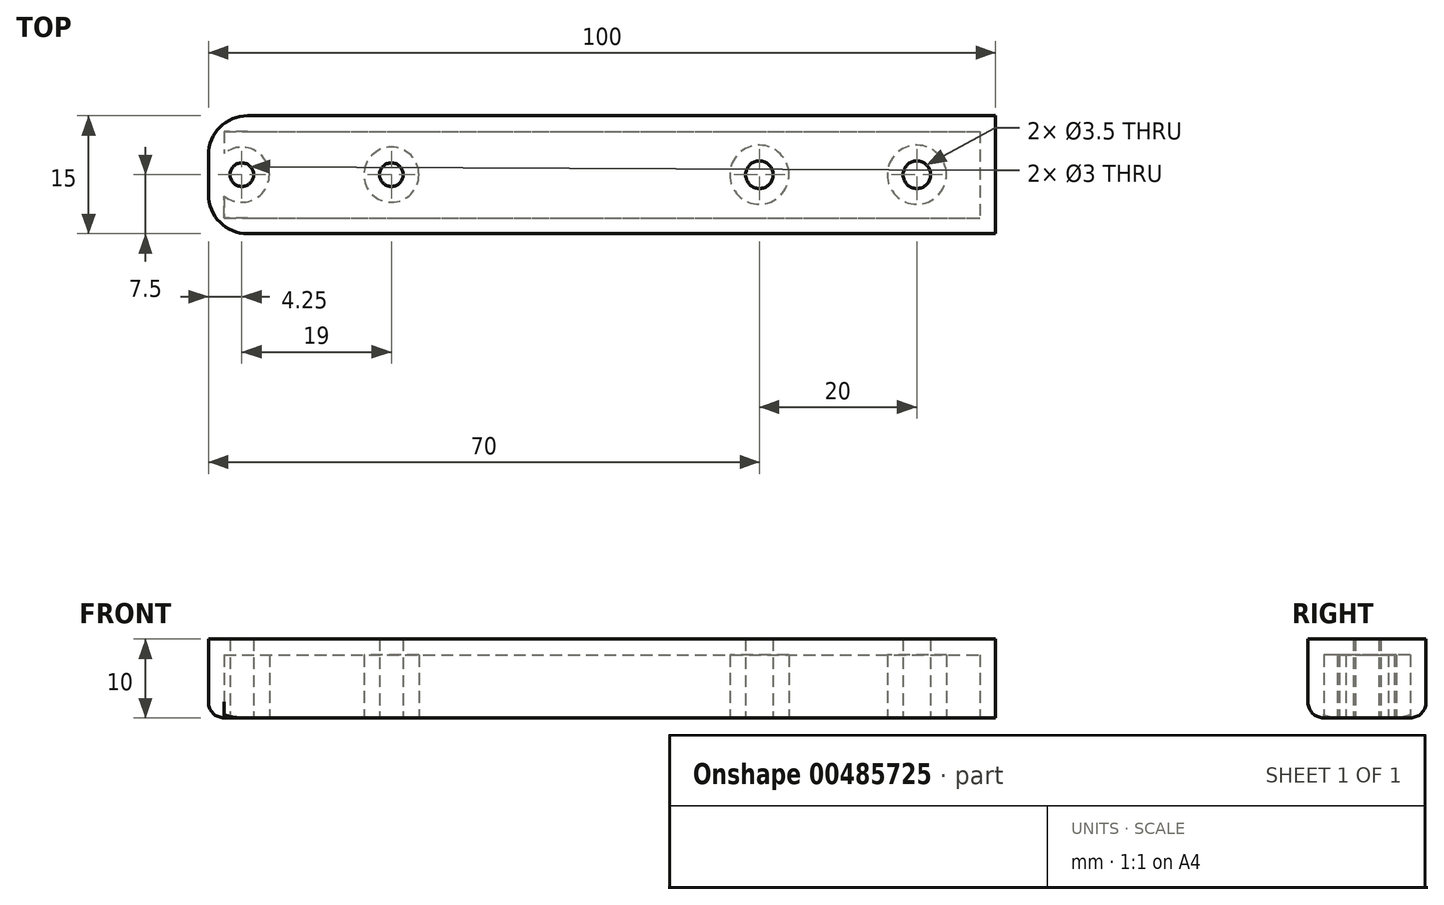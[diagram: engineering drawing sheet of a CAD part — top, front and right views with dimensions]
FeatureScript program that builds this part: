
annotation { "Feature Type Name" : "Feature", "Feature Type Description" : "" }
export const myFeature = defineFeature(function(context is Context, id is Id, definition is map)
    precondition{}
    {
        {
            var Q0;
            Q0=qCreatedBy(makeId("Top.planeOp"),FACE);
            var sketch = newSketch(context, id + "F0", { "sketchPlane" : qUnion([Q0])});
            skLineSegment(sketch, "E0.bottom", {"start": v(-50, 7.5) * mm, "end": v(50, 7.5) * mm});
            skLineSegment(sketch, "E0.top", {"start": v(-50, -7.5) * mm, "end": v(50, -7.5) * mm});
            skLineSegment(sketch, "E0.left", {"start": v(-50, 7.5) * mm, "end": v(-50, -7.5) * mm});
            skLineSegment(sketch, "E0.right", {"start": v(50, 7.5) * mm, "end": v(50, -7.5) * mm});
            skPoint(sketch, "E0.middle", {"position": v(0, 0) * mm});
            skCircle(sketch, "E1", {"center": v(40, 0) * mm, "radius": 1.75 * mm});
            skCircle(sketch, "E2", {"center": v(20, 0) * mm, "radius": 1.75 * mm});
            skCircle(sketch, "E3", {"center": v(-45.75, 0) * mm, "radius": 1.5 * mm});
            skCircle(sketch, "E4", {"center": v(-26.75, 0) * mm, "radius": 1.5 * mm});
            skLineSegment(sketch, "E5", {"start": v(10, 7.5) * mm, "end": v(10, -7.5) * mm});
            skSolve(sketch);
        }
        {
            var Q0;
            Q0=makeQuery(id+"F0.imprint","IMPRINT",FACE,{"disambiguationData":[TD([[makeQuery(id+"F0.imprint","IMPRINT",EDGE,{"derivedFrom":sQuery(id+"F0.wireOp",EDGE,"E0.bottom")}),-1.0]])]});
            extrude(context, id + "F1", {"entities" : qUnion([Q0]), "depth" : 10 * mm, "offsetDistance" : 25 * mm, "symmetric" : true});
        }
        {
            var Q0;
            Q0=makeQuery(id+"F1.opExtrude","CAP_FACE",FACE,{"disambiguationData":[OSD([sQuery(id+"F0.wireOp",EDGE,"E0.bottom"),sQuery(id+"F0.wireOp",EDGE,"E0.top"),sQuery(id+"F0.wireOp",EDGE,"E0.left"),sQuery(id+"F0.wireOp",EDGE,"E0.right")])],"isStart":true});
            shell(context, id + "F2", {"entities" : qUnion([Q0]), "thickness" : 2 * mm});
        }
        {
            var Q0;
            Q0=makeQuery(id+"F1.opExtrude","SWEPT_EDGE",EDGE,{"disambiguationData":[OSD([sQuery(id+"F0.wireOp",EDGE,"E0.top"),sQuery(id+"F0.wireOp",EDGE,"E0.left")])]});
            fillet(context, id + "F3", {"entities" : qUnion([Q0]), "radius" : 5 * mm, "tangentPropagation" : true, "allowEdgeOverflow" : false});
        }
        {
            var Q0;
            Q0=makeQuery(id+"F1.opExtrude","SWEPT_EDGE",EDGE,{"disambiguationData":[OSD([sQuery(id+"F0.wireOp",EDGE,"E0.bottom"),sQuery(id+"F0.wireOp",EDGE,"E0.left")])]});
            fillet(context, id + "F4", {"entities" : qUnion([Q0]), "radius" : 5 * mm, "tangentPropagation" : true, "allowEdgeOverflow" : false});
        }
        {
            var Q0;
            Q0=makeQuery(id+"F1.opExtrude","CAP_EDGE",EDGE,{"disambiguationData":[OSD([sQuery(id+"F0.wireOp",EDGE,"E0.top")])],"isStart":true});
            fillet(context, id + "F5", {"entities" : qUnion([Q0]), "radius" : 2 * mm, "tangentPropagation" : true, "allowEdgeOverflow" : false});
        }
        {
            var Q0;
            Q0=makeQuery(id+"F1.opExtrude","SWEPT_BODY",BODY,{"disambiguationData":[OSD([sQuery(id+"F0.wireOp",EDGE,"E0.bottom"),sQuery(id+"F0.wireOp",EDGE,"E0.top"),sQuery(id+"F0.wireOp",EDGE,"E0.left"),sQuery(id+"F0.wireOp",EDGE,"E0.right"),sQuery(id+"F0.wireOp",EDGE,"E1"),sQuery(id+"F0.wireOp",EDGE,"E2"),sQuery(id+"F0.wireOp",EDGE,"E3"),sQuery(id+"F0.wireOp",EDGE,"E4")])]});
            transform(context, id + "F6", {"entities" : qUnion([Q0]), "transformType" : TransformType.TRANSLATION_3D, "dx" : 0 * mm, "dy" : 0 * mm, "dz" : 0 * mm, "makeCopy" : true});
        }
        {
            var Q0;
            Q0=makeQuery(id+"F1.opExtrude","SWEPT_BODY",BODY,{"disambiguationData":[OSD([sQuery(id+"F0.wireOp",EDGE,"E0.bottom"),sQuery(id+"F0.wireOp",EDGE,"E0.top"),sQuery(id+"F0.wireOp",EDGE,"E0.left"),sQuery(id+"F0.wireOp",EDGE,"E0.right"),sQuery(id+"F0.wireOp",EDGE,"E1"),sQuery(id+"F0.wireOp",EDGE,"E2"),sQuery(id+"F0.wireOp",EDGE,"E3"),sQuery(id+"F0.wireOp",EDGE,"E4")])]});
            deleteBodies(context, id + "F7", {"entities" : qUnion([Q0])});
        }
    });
